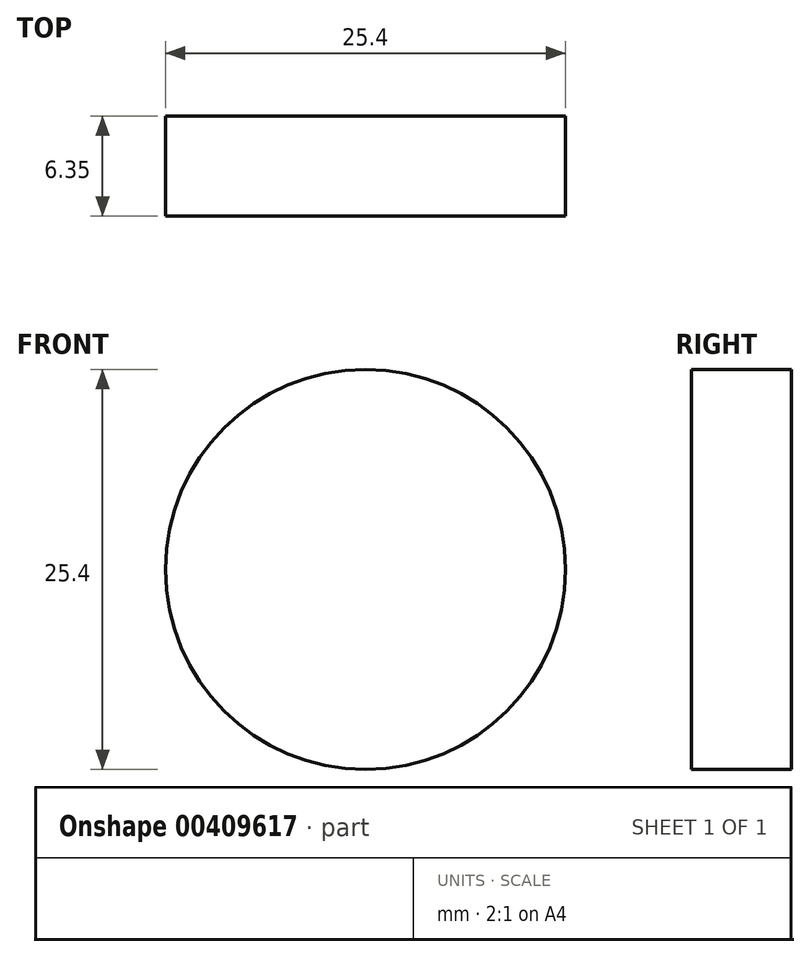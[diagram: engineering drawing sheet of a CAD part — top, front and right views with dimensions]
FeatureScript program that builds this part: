
annotation { "Feature Type Name" : "Feature", "Feature Type Description" : "" }
export const myFeature = defineFeature(function(context is Context, id is Id, definition is map)
    precondition{}
    {
        {
            var Q0;
            Q0=qCreatedBy(makeId("Front.planeOp"),FACE);
            var sketch = newSketch(context, id + "F0", { "sketchPlane" : qUnion([Q0])});
            skCircle(sketch, "E0", {"center": v(0, 0) * mm, "radius": 12.7 * mm});
            skSolve(sketch);
        }
        {
            var Q0;
            Q0 = qSketchRegion(id + "F0", true);
            extrude(context, id + "F1", {"entities" : qUnion([Q0]), "depth" : 6.35 * mm});
        }
    });
